# Revit family: Bloom Barstool Swivel Base
name_source: partatom
category: Furniture
revit_build: Autodesk Revit 2017 (Build: 20160225_1515(x64)
units: mm (PartAtom-declared; Revit-internal decimal feet)

## family parameters
Always vertical = Yes
Cut with Voids When Loaded = No
OmniClass Number = 23.40.20.00
OmniClass Title = General Furniture and Specialties
Room Calculation Point = No
Shared = No
Work Plane-Based = No

## types (1)
- Bloom Barstool Swivel Base
    Assembly Code = E2020200
    Assistance = Call for assistance number: 336.941.3446
    Barstool type = Swivel, Bar Height
    Collection = Bloom
    Depth = 20 mm
    Description = Barstool fully upholstered and Chrome swivel base
    Height = 43 mm  [stored 0.141076 ft]
    Industry = Restaurant, Lounge, Hotel, Club
    Length = 21 mm
    Manufacturer = Beaufurn
    Manufacturer Country = USA
    Model = Bloom Barstool Swivel Base
    Products of collection = Bloom Side Chair, Bloom Arm Chair, Bloom Lounge Chair and Bloom Barstools
    Seat depth = 18 mm  [stored 0.0590551 ft]
    Seat height = 30 mm  [stored 0.0984252 ft]
    Structure material = Steel
    Type Comments = Barstool ideal for Restaurants, Hotels and Universities
    URL = http://beaufurn.com
    Upholstery material = Graded Fabric or Com
    Usage = Indoor
    Yardage = 2 mm  [stored 0.00656168 ft]

note: [stored X ft] marks values corroborated as IEEE doubles in the binary element streams (Revit-internal decimal feet)

## geometry (parser evidence)
native form markers: Sweep x3
no freeform markers — native parametric forms only
